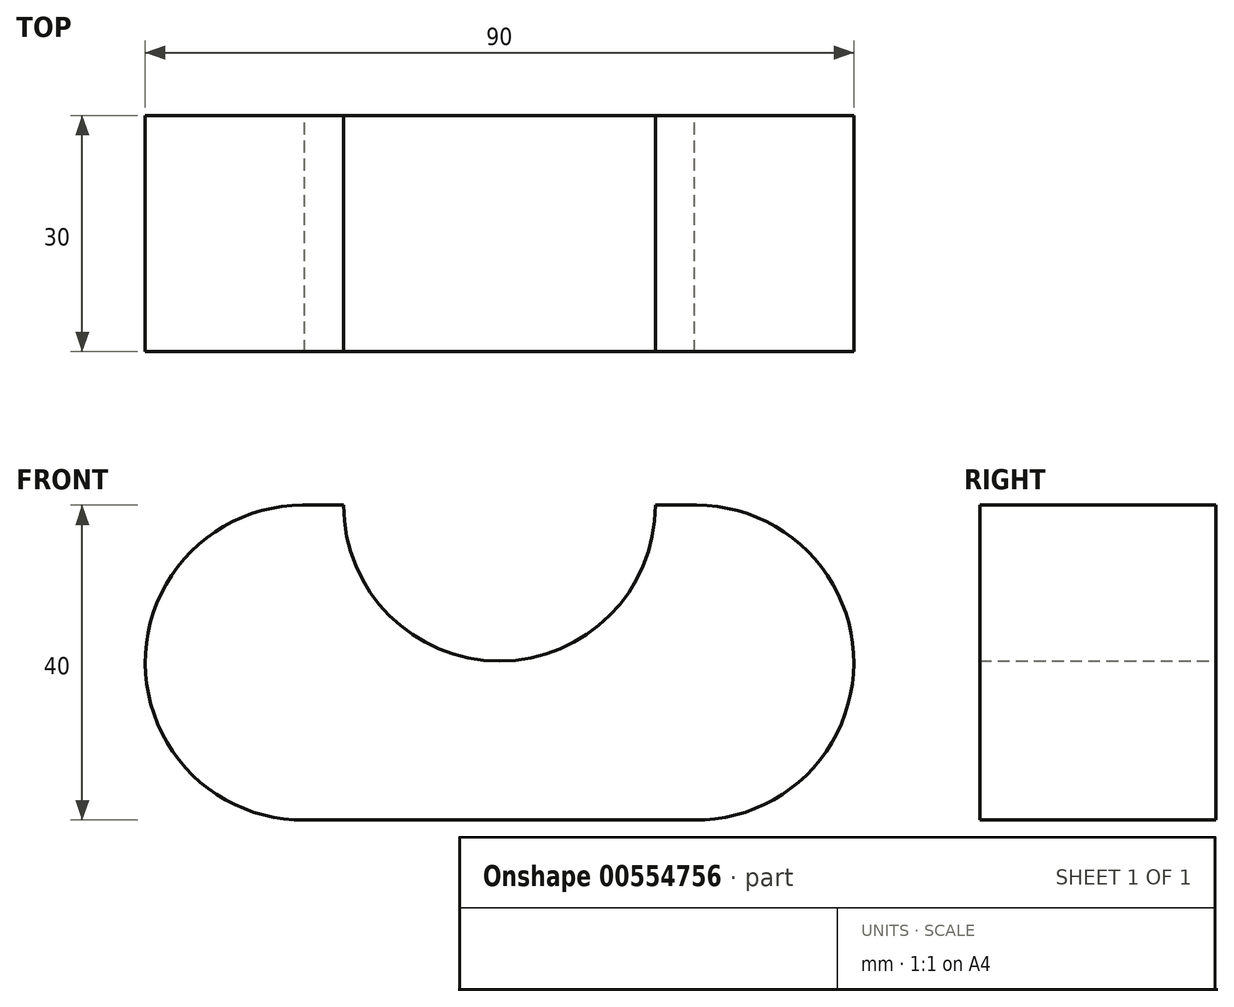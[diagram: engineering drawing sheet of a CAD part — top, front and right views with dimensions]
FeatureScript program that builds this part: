
annotation { "Feature Type Name" : "Feature", "Feature Type Description" : "" }
export const myFeature = defineFeature(function(context is Context, id is Id, definition is map)
    precondition{}
    {
        {
            var Q0;
            Q0=qCreatedBy(makeId("Front.planeOp"),FACE);
            var sketch = newSketch(context, id + "F0", { "sketchPlane" : qUnion([Q0])});
            skArc(sketch, "E0", {"start": v(-25, 20) * mm, "mid": v(-45, -0.13) * mm, "end": v(-24.74, -20) * mm});
            skLineSegment(sketch, "E1", {"start": v(-25.26, -20) * mm, "end": v(24.74, -20) * mm});
            skArc(sketch, "E2", {"start": v(24.74, -20) * mm, "mid": v(45, -0.13) * mm, "end": v(25, 20) * mm});
            skLineSegment(sketch, "E3", {"start": v(-25, 20) * mm, "end": v(-20, 20) * mm});
            skLineSegment(sketch, "E4", {"start": v(25, 20) * mm, "end": v(20, 20) * mm});
            skLineSegment(sketch, "E5", {"start": v(-20, 20) * mm, "end": v(-19.8, 20) * mm});
            skLineSegment(sketch, "E6", {"start": v(19.8, 20) * mm, "end": v(20, 20) * mm});
            skArc(sketch, "E7", {"start": v(-19.8, 20) * mm, "mid": v(0, 0.2) * mm, "end": v(19.8, 20) * mm});
            skSolve(sketch);
        }
        {
            var Q0;
            Q0 = qSketchRegion(id + "F0", true);
            var Q1;
            {var subQ0=sQuery(id+"F0.wireOp",EDGE,"E2");Q1=makeQuery(id+"F0.imprint","IMPRINT",FACE,{"disambiguationData":[TD([[makeQuery(id+"F0.imprint","IMPRINT",EDGE,{"derivedFrom":subQ0}),1.0]])]});}
            extrude(context, id + "F1", {"entities" : qUnion([Q0, Q1]), "depth" : 30 * mm, "offsetDistance" : 25 * mm});
        }
    });
